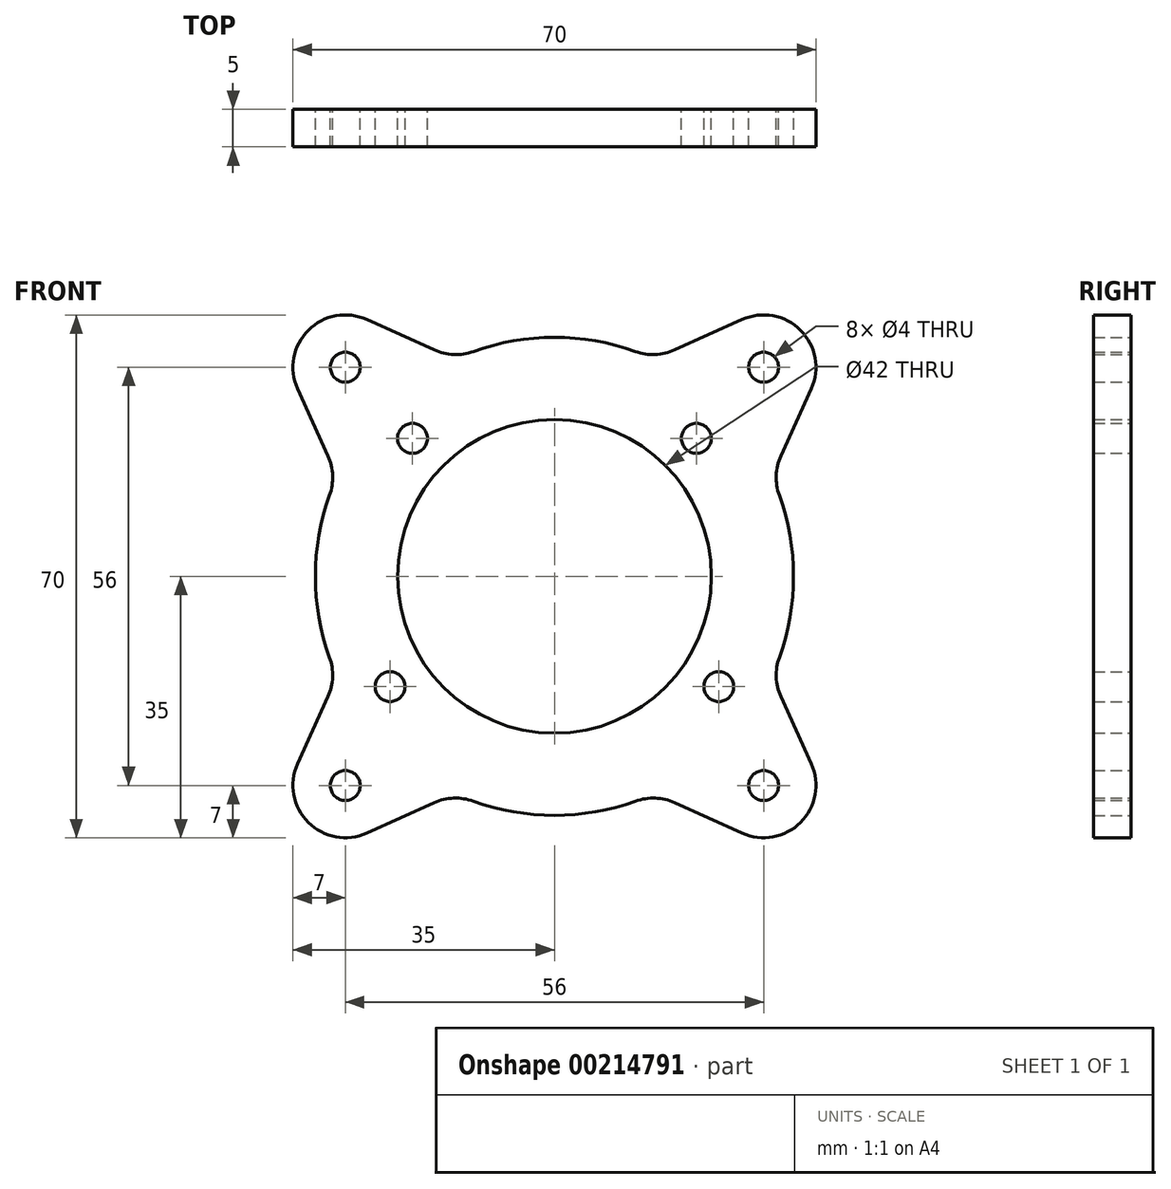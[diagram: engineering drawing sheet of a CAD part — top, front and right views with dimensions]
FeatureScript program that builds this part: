
annotation { "Feature Type Name" : "Feature", "Feature Type Description" : "" }
export const myFeature = defineFeature(function(context is Context, id is Id, definition is map)
    precondition{}
    {
        {
            var Q0;
            Q0=qCreatedBy(makeId("Front.planeOp"),FACE);
            var sketch = newSketch(context, id + "F0", { "sketchPlane" : qUnion([Q0])});
            skCircle(sketch, "E0", {"center": v(0, 0) * mm, "radius": 21 * mm});
            skCircle(sketch, "E1", {"center": v(-19, 18.47) * mm, "radius": 2 * mm});
            skCircle(sketch, "E2", {"center": v(19, 18.47) * mm, "radius": 2 * mm});
            skCircle(sketch, "E3", {"center": v(22, -14.77) * mm, "radius": 2 * mm});
            skCircle(sketch, "E4", {"center": v(-22, -14.77) * mm, "radius": 2 * mm});
            skCircle(sketch, "E5", {"center": v(-28, 28) * mm, "radius": 2 * mm});
            skCircle(sketch, "E6", {"center": v(28, 28) * mm, "radius": 2 * mm});
            skCircle(sketch, "E7", {"center": v(28, -28) * mm, "radius": 2 * mm});
            skCircle(sketch, "E8", {"center": v(-28, -28) * mm, "radius": 2 * mm});
            skCircle(sketch, "E9", {"center": v(0, 0) * mm, "radius": 26.5 * mm, "construction": true});
            skLineSegment(sketch, "E10", {"start": v(-34.38, 25.12) * mm, "end": v(-30.3, 16.1) * mm});
            skLineSegment(sketch, "E11", {"start": v(-34.38, -25.12) * mm, "end": v(-30.3, -16.1) * mm});
            skLineSegment(sketch, "E12", {"start": v(-25.12, -34.38) * mm, "end": v(-16.1, -30.3) * mm});
            skLineSegment(sketch, "E13", {"start": v(-25.12, 34.38) * mm, "end": v(-16.1, 30.3) * mm});
            skLineSegment(sketch, "E14", {"start": v(25.12, 34.38) * mm, "end": v(16.1, 30.3) * mm});
            skLineSegment(sketch, "E15", {"start": v(34.38, -25.12) * mm, "end": v(30.3, -16.1) * mm});
            skLineSegment(sketch, "E16", {"start": v(25.12, -34.38) * mm, "end": v(16.1, -30.3) * mm});
            skLineSegment(sketch, "E17", {"start": v(34.38, 25.12) * mm, "end": v(30.3, 16.1) * mm});
            skArc(sketch, "E18", {"start": v(-30.1, 10.85) * mm, "mid": v(-32, 0) * mm, "end": v(-30.1, -10.85) * mm});
            skArc(sketch, "E19", {"start": v(-10.85, -30.1) * mm, "mid": v(0, -32) * mm, "end": v(10.85, -30.1) * mm});
            skArc(sketch, "E20", {"start": v(30.1, -10.85) * mm, "mid": v(32, 0) * mm, "end": v(30.1, 10.85) * mm});
            skArc(sketch, "E21", {"start": v(10.85, 30.1) * mm, "mid": v(0, 32) * mm, "end": v(-10.85, 30.1) * mm});
            skArc(sketch, "E22", {"start": v(-34.38, -25.12) * mm, "mid": v(-32.95, -32.95) * mm, "end": v(-25.12, -34.38) * mm});
            skArc(sketch, "E23", {"start": v(-25.12, 34.38) * mm, "mid": v(-32.95, 32.95) * mm, "end": v(-34.38, 25.12) * mm});
            skArc(sketch, "E24", {"start": v(34.38, 25.12) * mm, "mid": v(32.95, 32.95) * mm, "end": v(25.12, 34.38) * mm});
            skArc(sketch, "E25", {"start": v(25.12, -34.38) * mm, "mid": v(32.95, -32.95) * mm, "end": v(34.38, -25.12) * mm});
            skPoint(sketch, "E26.visualSharp", {"position": v(-29.07, 13.37) * mm});
            skArc(sketch, "E26.filletArc", {"start": v(-30.1, 10.85) * mm, "mid": v(-29.7, 13.5) * mm, "end": v(-30.3, 16.1) * mm});
            skPoint(sketch, "E27.visualSharp", {"position": v(-29.07, -13.37) * mm});
            skArc(sketch, "E27.filletArc", {"start": v(-30.3, -16.1) * mm, "mid": v(-29.7, -13.5) * mm, "end": v(-30.1, -10.85) * mm});
            skPoint(sketch, "E28.visualSharp", {"position": v(-13.37, -29.07) * mm});
            skArc(sketch, "E28.filletArc", {"start": v(-10.85, -30.1) * mm, "mid": v(-13.5, -29.7) * mm, "end": v(-16.1, -30.3) * mm});
            skPoint(sketch, "E29.visualSharp", {"position": v(13.37, -29.07) * mm});
            skArc(sketch, "E29.filletArc", {"start": v(16.1, -30.3) * mm, "mid": v(13.5, -29.7) * mm, "end": v(10.85, -30.1) * mm});
            skPoint(sketch, "E30.visualSharp", {"position": v(29.07, -13.37) * mm});
            skArc(sketch, "E30.filletArc", {"start": v(30.1, -10.85) * mm, "mid": v(29.7, -13.5) * mm, "end": v(30.3, -16.1) * mm});
            skPoint(sketch, "E31.visualSharp", {"position": v(29.07, 13.37) * mm});
            skArc(sketch, "E31.filletArc", {"start": v(30.3, 16.1) * mm, "mid": v(29.7, 13.5) * mm, "end": v(30.1, 10.85) * mm});
            skPoint(sketch, "E32.visualSharp", {"position": v(-13.37, 29.07) * mm});
            skArc(sketch, "E32.filletArc", {"start": v(-16.1, 30.3) * mm, "mid": v(-13.5, 29.7) * mm, "end": v(-10.85, 30.1) * mm});
            skPoint(sketch, "E33.visualSharp", {"position": v(13.37, 29.07) * mm});
            skArc(sketch, "E33.filletArc", {"start": v(10.85, 30.1) * mm, "mid": v(13.5, 29.7) * mm, "end": v(16.1, 30.3) * mm});
            skSolve(sketch);
        }
        {
            var Q0;
            Q0 = qSketchRegion(id + "F0", true);
            extrude(context, id + "F1", {"entities" : qUnion([Q0]), "depth" : 5 * mm});
        }
    });
